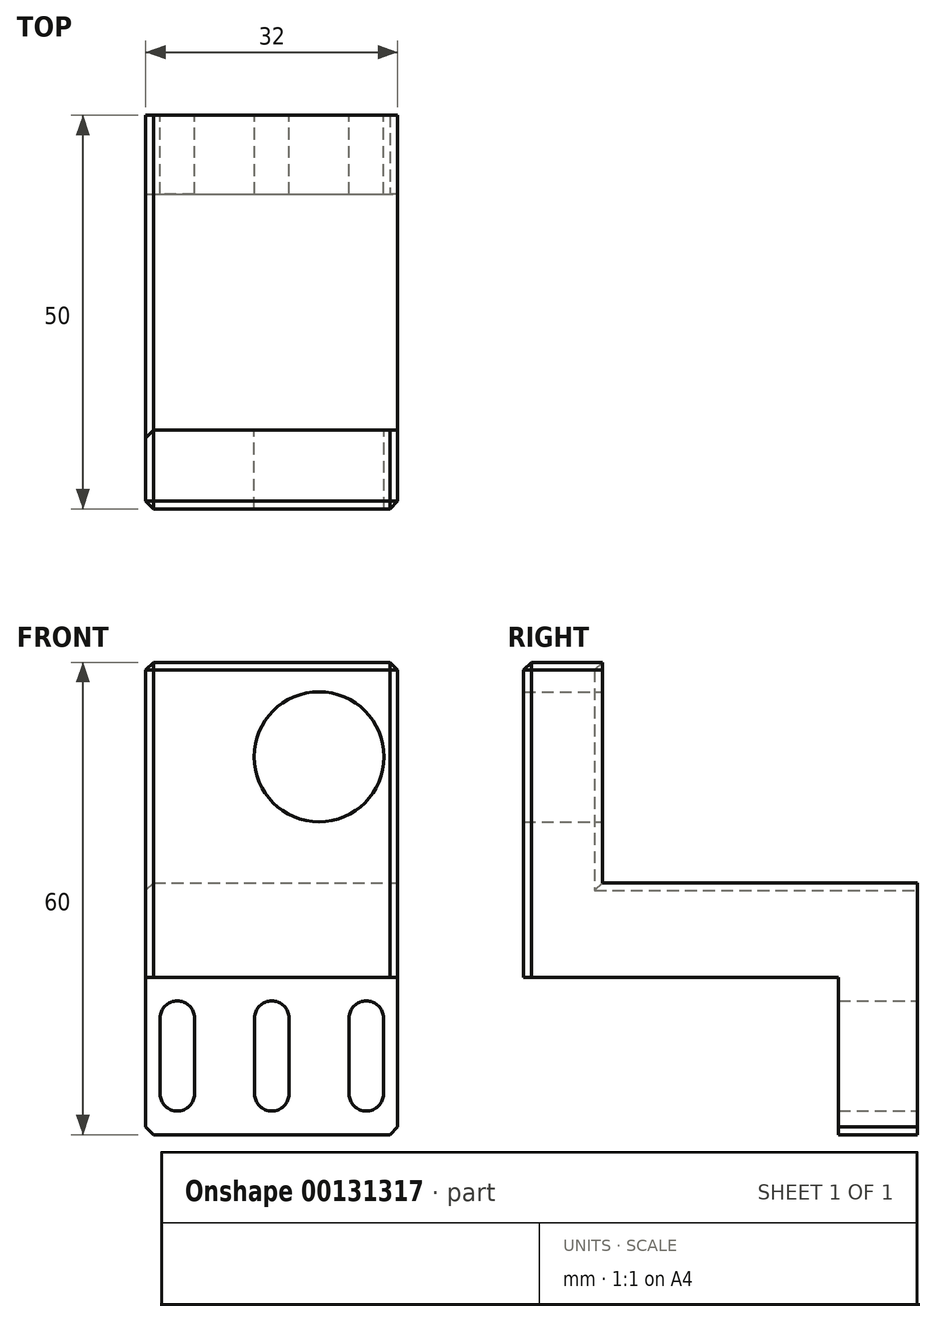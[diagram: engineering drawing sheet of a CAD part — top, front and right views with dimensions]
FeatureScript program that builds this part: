
annotation { "Feature Type Name" : "Feature", "Feature Type Description" : "" }
export const myFeature = defineFeature(function(context is Context, id is Id, definition is map)
    precondition{}
    {
        {
            var Q0;
            Q0=qCreatedBy(makeId("Front.planeOp"),FACE);
            var sketch = newSketch(context, id + "F0", { "sketchPlane" : qUnion([Q0])});
            skLineSegment(sketch, "E0.bottom", {"start": v(-22, -30) * mm, "end": v(10, -30) * mm});
            skLineSegment(sketch, "E0.top", {"start": v(-22, 30) * mm, "end": v(10, 30) * mm});
            skLineSegment(sketch, "E0.left", {"start": v(-10, -30) * mm, "end": v(-10, 30) * mm, "construction": true});
            skLineSegment(sketch, "E0.right", {"start": v(10, -30) * mm, "end": v(10, 30) * mm});
            skPoint(sketch, "E0.middle", {"position": v(0, 0) * mm});
            skCircle(sketch, "E1", {"center": v(0, 18) * mm, "radius": 8.25 * mm});
            skLineSegment(sketch, "E2.bottom", {"start": v(-8.17, -24.83) * mm, "end": v(-3.82, -24.83) * mm, "construction": true});
            skLineSegment(sketch, "E2.top", {"start": v(-8.17, -15.18) * mm, "end": v(-3.82, -15.18) * mm, "construction": true});
            skLineSegment(sketch, "E2.left", {"start": v(-8.17, -24.83) * mm, "end": v(-8.17, -15.18) * mm});
            skLineSegment(sketch, "E2.right", {"start": v(-3.82, -24.83) * mm, "end": v(-3.82, -15.18) * mm});
            skPoint(sketch, "E2.middle", {"position": v(-6, -20) * mm});
            skArc(sketch, "E3", {"start": v(-3.82, -15.18) * mm, "mid": v(-6, -13) * mm, "end": v(-8.17, -15.18) * mm});
            skArc(sketch, "E4", {"start": v(-8.17, -24.83) * mm, "mid": v(-6, -27) * mm, "end": v(-3.82, -24.83) * mm});
            skLineSegment(sketch, "E5", {"start": v(0, 30) * mm, "end": v(0, -30) * mm, "construction": true});
            skArc(sketch, "E6.MirrorCS", {"start": v(3.83, -15.18) * mm, "mid": v(6, -13) * mm, "end": v(8.18, -15.18) * mm});
            skLineSegment(sketch, "E7.MirrorCS", {"start": v(3.83, -24.83) * mm, "end": v(3.83, -15.18) * mm});
            skLineSegment(sketch, "E8.MirrorCS", {"start": v(8.18, -24.83) * mm, "end": v(8.18, -15.18) * mm});
            skArc(sketch, "E9.MirrorCS", {"start": v(8.18, -24.83) * mm, "mid": v(6, -27) * mm, "end": v(3.83, -24.83) * mm});
            skLineSegment(sketch, "E10.0", {"start": v(-22, -30) * mm, "end": v(-22, 30) * mm});
            skLineSegment(sketch, "E11.1.0.0", {"start": v(-20.17, -24.83) * mm, "end": v(-20.17, -15.18) * mm});
            skArc(sketch, "E11.1.0.1", {"start": v(-15.83, -15.18) * mm, "mid": v(-18, -13) * mm, "end": v(-20.18, -15.18) * mm});
            skArc(sketch, "E11.1.0.2", {"start": v(-20.18, -24.83) * mm, "mid": v(-18, -27) * mm, "end": v(-15.83, -24.83) * mm});
            skLineSegment(sketch, "E11.1.0.3", {"start": v(-15.82, -24.83) * mm, "end": v(-15.82, -15.18) * mm});
            skLineSegment(sketch, "E11.1.0.5", {"start": v(-2, -30) * mm, "end": v(-2, 30) * mm});
            skLineSegment(sketch, "E11.direction1", {"start": v(-8.17, -24.83) * mm, "end": v(-20.18, -24.83) * mm, "construction": true});
            skSolve(sketch);
        }
        {
            var Q0;
            Q0 = qSketchRegion(id + "F0", true);
            extrude(context, id + "F1", {"entities" : qUnion([Q0]), "depth" : 50 * mm});
        }
        {
            var Q0;
            Q0=makeQuery(id+"F1.opExtrude","SWEPT_FACE",FACE,{"disambiguationData":[OSD([sQuery(id+"F0.wireOp",EDGE,"E0.right")])]});
            var sketch = newSketch(context, id + "F2", { "sketchPlane" : qUnion([Q0])});
            skLineSegment(sketch, "E12.bottom", {"start": v(0, 30) * mm, "end": v(-40, 30) * mm});
            skLineSegment(sketch, "E12.top", {"start": v(0, 2) * mm, "end": v(-40, 2) * mm});
            skLineSegment(sketch, "E12.left", {"start": v(0, 30) * mm, "end": v(0, 2) * mm});
            skLineSegment(sketch, "E12.right", {"start": v(-40, 30) * mm, "end": v(-40, 2) * mm});
            skPoint(sketch, "E13.0", {"position": v(-50, -30) * mm});
            skLineSegment(sketch, "E14.bottom", {"start": v(-50, -30) * mm, "end": v(-10, -30) * mm});
            skLineSegment(sketch, "E14.top", {"start": v(-50, -10) * mm, "end": v(-10, -10) * mm});
            skLineSegment(sketch, "E14.left", {"start": v(-50, -30) * mm, "end": v(-50, -10) * mm});
            skLineSegment(sketch, "E14.right", {"start": v(-10, -30) * mm, "end": v(-10, -10) * mm});
            skSolve(sketch);
        }
        {
            var Q0;
            Q0=makeQuery(id+"F2.imprint","IMPRINT",FACE,{"disambiguationData":[TD([[makeQuery(id+"F2.imprint","IMPRINT",EDGE,{"derivedFrom":sQuery(id+"F2.wireOp",EDGE,"E12.bottom")}),-1.0]])]});
            var Q1;
            Q1=makeQuery(id+"F2.imprint","IMPRINT",FACE,{"disambiguationData":[TD([[makeQuery(id+"F2.imprint","IMPRINT",EDGE,{"derivedFrom":sQuery(id+"F2.wireOp",EDGE,"E14.bottom")}),1.0]])]});
            extrude(context, id + "F3", {"entities" : qUnion([Q0, Q1]), "operationType" : NewBodyOperationType.REMOVE, "endBound" : BoundingType.THROUGH_ALL, "oppositeDirection" : true, "depth" : 25 * mm});
        }
        {
            var Q0;
            Q0=makeQuery(id+"F3.boolean.opBoolean","COPY",EDGE,{"derivedFrom":makeQuery(id+"F3.opExtrude","CAP_EDGE",EDGE,{"disambiguationData":[OSD([sQuery(id+"F2.wireOp",EDGE,"E12.top")])],"isStart":true})});
            var Q1;
            Q1=makeQuery(id+"F3.boolean.opBoolean","COPY",EDGE,{"derivedFrom":makeQuery(id+"F3.opExtrude","CAP_EDGE",EDGE,{"disambiguationData":[OSD([sQuery(id+"F2.wireOp",EDGE,"E12.right")])],"isStart":true})});
            var Q2;
            Q2=makeQuery(id+"F1.opExtrude","SWEPT_EDGE",EDGE,{"disambiguationData":[OSD([sQuery(id+"F0.wireOp",EDGE,"E0.top"),sQuery(id+"F0.wireOp",EDGE,"E0.right")])]});
            var Q3;
            Q3=makeQuery(id+"F1.opExtrude","CAP_EDGE",EDGE,{"disambiguationData":[OSD([sQuery(id+"F0.wireOp",EDGE,"E0.right")])],"isStart":false});
            var Q4;
            Q4=makeQuery(id+"F1.opExtrude","SWEPT_EDGE",EDGE,{"disambiguationData":[OSD([sQuery(id+"F0.wireOp",EDGE,"E0.bottom"),sQuery(id+"F0.wireOp",EDGE,"E0.right")])]});
            var Q5;
            Q5=makeQuery(id+"F1.opExtrude","CAP_EDGE",EDGE,{"disambiguationData":[OSD([sQuery(id+"F0.wireOp",EDGE,"E0.top")])],"isStart":false});
            var Q6;
            Q6=makeQuery(id+"F3.boolean.opBoolean","COPY",EDGE,{"derivedFrom":makeQuery(id+"F3.opExtrude","SWEPT_EDGE",EDGE,{"disambiguationData":[OSD([sQuery(id+"F0.wireOp",EDGE,"E0.top"),sQuery(id+"F0.wireOp",EDGE,"E0.right"),sQuery(id+"F2.wireOp",EDGE,"E12.right")])]})});
            var Q7;
            Q7=makeQuery(id+"F3.boolean.opBoolean","INTERSECT",EDGE,{"derivedFrom":[makeQuery(id+"F1.opExtrude","SWEPT_FACE",FACE,{"disambiguationData":[OSD([sQuery(id+"F0.wireOp",EDGE,"E10.0")])]}),makeQuery(id+"F3.opExtrude","SWEPT_FACE",FACE,{"disambiguationData":[OSD([sQuery(id+"F2.wireOp",EDGE,"E12.top")])]})]});
            var Q8;
            Q8=makeQuery(id+"F1.opExtrude","SWEPT_EDGE",EDGE,{"disambiguationData":[OSD([sQuery(id+"F0.wireOp",EDGE,"E0.bottom"),sQuery(id+"F0.wireOp",EDGE,"E10.0")])]});
            var Q9;
            Q9=makeQuery(id+"F1.opExtrude","CAP_EDGE",EDGE,{"disambiguationData":[OSD([sQuery(id+"F0.wireOp",EDGE,"E10.0")])],"isStart":false});
            var Q10;
            Q10=makeQuery(id+"F1.opExtrude","CAP_EDGE",EDGE,{"disambiguationData":[OSD([sQuery(id+"F0.wireOp",EDGE,"E0.bottom")])],"isStart":false});
            var Q11;
            Q11=makeQuery(id+"F1.opExtrude","SWEPT_EDGE",EDGE,{"disambiguationData":[OSD([sQuery(id+"F0.wireOp",EDGE,"E0.top"),sQuery(id+"F0.wireOp",EDGE,"E10.0")])]});
            var Q12;
            Q12=makeQuery(id+"F3.boolean.opBoolean","INTERSECT",EDGE,{"derivedFrom":[makeQuery(id+"F1.opExtrude","SWEPT_FACE",FACE,{"disambiguationData":[OSD([sQuery(id+"F0.wireOp",EDGE,"E10.0")])]}),makeQuery(id+"F3.opExtrude","SWEPT_FACE",FACE,{"disambiguationData":[OSD([sQuery(id+"F2.wireOp",EDGE,"E12.right")])]})]});
            var Q13;
            Q13=makeQuery(id+"F3.boolean.opBoolean","COPY",EDGE,{"derivedFrom":makeQuery(id+"F3.opExtrude","SWEPT_EDGE",EDGE,{"disambiguationData":[OSD([sQuery(id+"F0.wireOp",EDGE,"E0.right"),sQuery(id+"F2.wireOp",EDGE,"E14.top"),sQuery(id+"F2.wireOp",EDGE,"E14.left")])]})});
            chamfer(context, id + "F4", {"entities" : qUnion([Q0, Q1, Q2, Q3, Q4, Q5, Q6, Q7, Q8, Q9, Q10, Q11, Q12, Q13]), "width" : 1 * mm, "tangentPropagation" : true});
        }
    });
